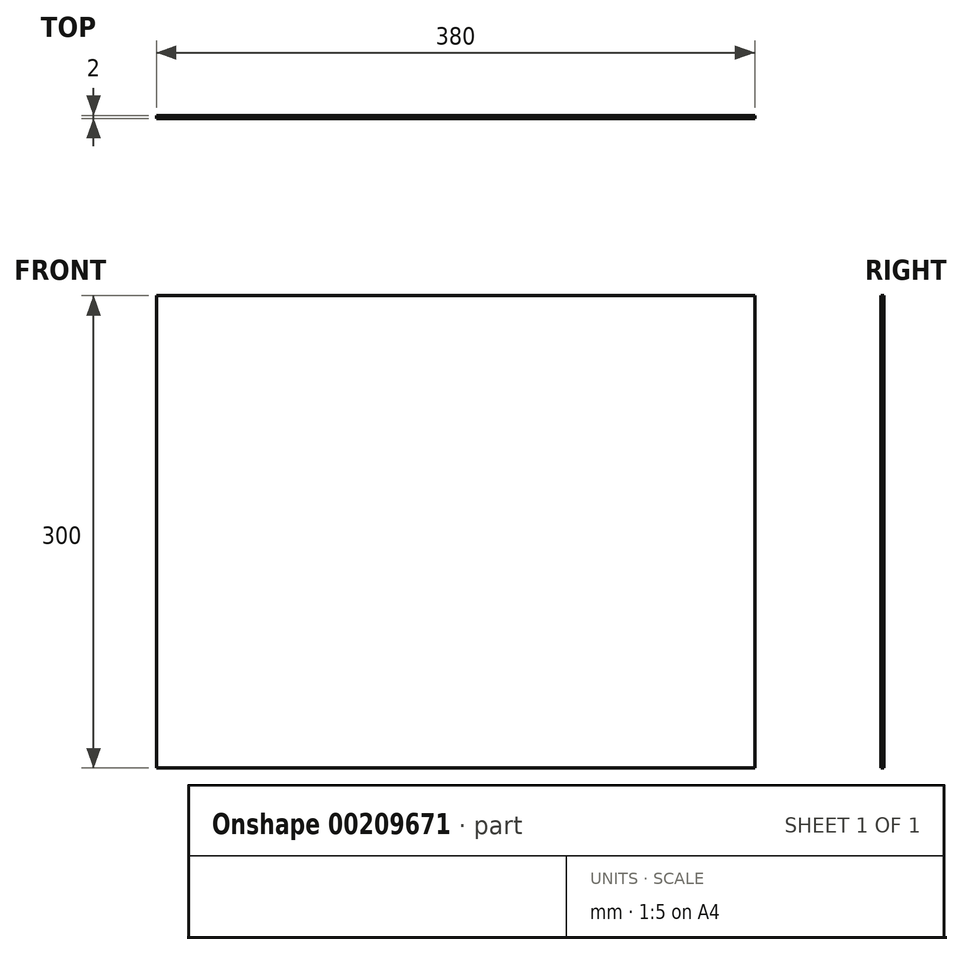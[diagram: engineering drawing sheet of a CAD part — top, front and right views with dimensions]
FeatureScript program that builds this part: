
annotation { "Feature Type Name" : "Feature", "Feature Type Description" : "" }
export const myFeature = defineFeature(function(context is Context, id is Id, definition is map)
    precondition{}
    {
        {
            var Q0;
            Q0=qCreatedBy(makeId("Front.planeOp"),FACE);
            var sketch = newSketch(context, id + "F0", { "sketchPlane" : qUnion([Q0])});
            skLineSegment(sketch, "E0.bottom", {"start": v(-412, 324.79) * mm, "end": v(-32, 324.79) * mm});
            skLineSegment(sketch, "E0.top", {"start": v(-412, 24.79) * mm, "end": v(-32, 24.79) * mm});
            skLineSegment(sketch, "E0.left", {"start": v(-412, 324.79) * mm, "end": v(-412, 24.79) * mm});
            skLineSegment(sketch, "E0.right", {"start": v(-32, 324.79) * mm, "end": v(-32, 24.79) * mm});
            skSolve(sketch);
        }
        {
            var Q0;
            Q0=makeQuery(id+"F0.imprint","IMPRINT",FACE,{"disambiguationData":[TD([[makeQuery(id+"F0.imprint","IMPRINT",EDGE,{"derivedFrom":sQuery(id+"F0.wireOp",EDGE,"E0.bottom")}),-1.0]])]});
            extrude(context, id + "F1", {"entities" : qUnion([Q0]), "depth" : 2 * mm});
        }
    });
